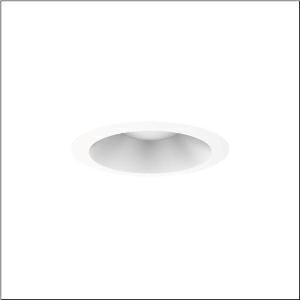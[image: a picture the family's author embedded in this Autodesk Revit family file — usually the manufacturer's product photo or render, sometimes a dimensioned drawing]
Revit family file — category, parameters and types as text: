
# Revit family: lunis_31_midi_51dn16dg42
name_source: partatom
category: Lighting Fixtures
units: mm (PartAtom-declared; Revit-internal decimal feet)

## family parameters
Cut with Voids When Loaded = No
Host = Face
Light Source = No
Part Type = Normal
Room Calculation Point = No
Round Connector Dimension = Use Diameter
Shared = No

## types (1)
- Lunis 31 midi (1 x LED, 2150 lm, 17 W, 4000K)
    Apparent Load = 17 VA
    CIE Flux Codes = 64 93 99 100 100
    Color Rendering = 80
    Color Temperature = 4000K
    Default Elevation = 1800 mm
    Description = Lunis 31,  midi, downlight, light control with reflector, light emission: direct distribution, LED rated luminous flux: 2.150lm, light colour: 840, mains connection: 220..240V, AC, 50/60Hz, housing, white, protection rating (complete): IP20, protection rating (on room side): IP54, insulation class (complete): insulation class II (safety insulation), certification: CE, packaging unit: 1 piece
    Height = 0 mm  [stored 0 ft]
    Lamp = 1 x LED
    Lamp Light Flux = 2150 lm
    Lamp Power = 17 W
    Lamp count = 1
    Length = 259 mm
    Luminous efficacy = 126 lm/W
    Manufacturer = Siteco
    ModVariant = No
    Model = 51DN16DG42
    Mounting Place = Ceiling
    Mounting Type = Recessed
    Number of Poles = 1
    OnlyDefault = Yes
    Power Factor = 1
    Product Name = Lunis 31 midi
    Product group = downlight
    ProductGroupID = 400
    Protection Class = Protection class II
    Protection Degree = IP 20
    RLX_Detail_Level = 1
    RLX_Emergency_Light_Flux = 0 lm
    RLX_Emergency_Type = 0
    RLX_Emergency_Type_DB = No
    RlxData = <blob elided: 23765 chars, md5=7d514361>
    Socket = socket
    Standby Power = 0 W
    System Light Flux = 2150 lm
    System Power = 17 W
    Type Comments = Product without accessories
    Type Image = l_1006711.jpg
    URL = http://relux.com
    VarID = ---
    Voltage = 0 V
    Weight = 0.00 kg
    Width = 0 mm  [stored 0 ft]

note: [stored X ft] marks values corroborated as IEEE doubles in the binary element streams (Revit-internal decimal feet)

## geometry (parser evidence)
native form markers: Blend x4, Sweep x11
no freeform markers — native parametric forms only
